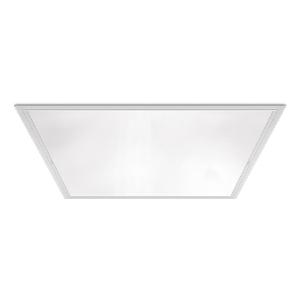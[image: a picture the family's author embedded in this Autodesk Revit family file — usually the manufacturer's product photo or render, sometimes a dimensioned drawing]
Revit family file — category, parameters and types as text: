
# Revit family: 3f_filippi_-_l_340_luce_diffusa_lgs_ip65v_3f_filippi_-_24000_-_l_340_29w-940_dali_lgs_ip65v_596x596
name_source: partatom
category: Lighting Fixtures
units: mm (PartAtom-declared; Revit-internal decimal feet)

## family parameters
Cut with Voids When Loaded = No
Host = Face
Light Source = No
Part Type = Normal
Room Calculation Point = No
Round Connector Dimension = Use Diameter
Shared = No

## types (1)
- 3F Filippi - L 340 Luce Diffusa LGS IP65V (1 x LED, 3413 lm, 35 W, 4000 K)
    Apparent Load = 35 VA
    Approval mark = ENEC
    CIE Flux Codes = 67 92 98 100 100
    Color Rendering = 90
    Color Temperature = 4000 K
    Control Gear = Electronic transformer
    Default Elevation = 1800 mm
    Description = ILLUMINOTECHNICAL
Luminous efficiency 100% (DLOR 100%, ULOR 0%).
Initial luminous flux of the luminaire 3413 lm.
Direct symmetric distribution.
Installation Interdistance Transv.D = 1.19 x hu - Long.D = 1.17 x hu.
Average luminance <1500 cd/m² for radial angles >65°.
Tabular UGR (CIE 117 - 4H-8H; S=0.25H; 70/50/20): RUG 16 - 16.1.
Beam angle: 87° - 86°.
Luminous efficacy 98 lm/W.
Lifetime (L93/B10): 30000 h. (tq+25°C)
Lifetime (L90/B10): 50000 h. (tq+25°C)
Lifetime (L85/B10): 80000 h. (tq+25°C)
Lifetime (L80/B10): 100000 h. (tq+25°C)
Sudden decreased luminous flux after 50000 hours: 0% (C0).
Photobiological safety in compliance with IEC/TR 62778: RG0 risk exempt, (IEC 62471).
In compliance with IEC/EN 62722-2-1 - IEC/EN 62717 standards.

SOURCE
Squared LED module 29W/940.
Energy efficiency class (UE 2019/2020 - UE 2019/2015): D.
CIE 13.3 Colour rendering index: CRI >90 (R9 >50%).
IES TM-30 Fidelity Index: Rf = 92 Rg = 101.
CCT nominal colour temperature 4000 K.
Colour initial tolerance (MacAdam): SDCM 3.

MECHANICAL
Housing in hot-galvanised steel, painted in white polyester.
Perimetral frame in white polycarbonate.
LGS micro-prismatic flat diffuser in transparent methacrylate (PMMA), multi-lenticular exterior, anti-glare.
Anti-glare opal polycarbonate filter for brightness uniformity.
Luminaire with limited surface temperature. - D - (EN 60598-2-24)
Dimensions: 596x596 mm, height 80 mm. Weight 4.45 kg.
IP65 protection degree for exposed part, IP40 for recessed part.
Mechanical strength to impacts IK06 (1 joule).
Glow-wire test resistance 650°C.

ELECTRICAL
Wiring on a separate unit.
Halogen Free DALI-2 DATI (Parts 251, 252, 253), PUSH-DIM, electronic wiring 230V-50/60Hz, power factor 0.95 at full load, THD <25%, constant output current, SELV, class II, 1 driver, 1 DALI addresse.
Power of the luminaire 35 W.
CE - IEC 60598-1 - EN 60598-1.
SAFE FLICKER: PstLM=<1 and SVM=<0.4 (IEC TR 61547-1 and IEC TR 63158), to ensure a more comfortable and safe light.
Luminaire compliant with EN 60598-2-22 for power supply from a centralised emergency system CPSS (Central Power Supply System), not incorporated in the luminaire - high risk areas excluded. The default power and flux are 100% in AC and 100% in DC.
Ambient temperature from 0°C to +40°C.
Temperature class T6 max 85°C.
Relative humidity UR: <85%.

INSTALLATION
Lay-on or pull-up recessed fitting using frame accessory.
All accessories dedicated to this product are available on the Catalog and on our website www.3F-Filippi.com.

APPLICATIONS
Suitable product for food production plants (HACCP), IFS (Food Version 6), BRC (GSFS Food Version 7).
In environments requiring protection and simplified cleaning.
Hospitals, pharmaceutical, chemical, aseptic laboratories, sterilised rooms.
Environments: with VDTs, meeting rooms, offices.
Environments: architectural, commercial, staterooms, banks.
Environments where demanding visual tasks are performed and soft diffuse light is required for optimal visual comfort and total shielding of the light source.

LIGHT MANAGEMENT
Recommended minimum setting: 10%.
The luminaire, equipped with (DALI-2 DATI) driver, can be controlled manually with 3F Easy Dim technology or automatically/manually with wired or wireless DALI/D2D control systems.
The D2D driver guarantees interoperability with other devices with the same certification by making the following information available:
Device Data (Part 251), Energy Report (Part 252), Diagnosis & Maintenance (Part 253).
In electrical systems without a regulation system (manual or automatic) and DALI bus, a suitable jumper must be made on the DA-DA terminals of the appliance.

WARNING
Luminaire designed for disposal/recycling at end-of-life.
Replaceable (LED only) light source by a professional. Replaceable control gear by a professional.
    Height = 0 mm  [stored 0 ft]
    Lamp = 1 x LED
    Lamp Light Flux = 3413 lm
    Lamp Power = 35 W
    Lamp count = 1
    Length = 596 mm
    Lifetime = 50000 h
    Luminous efficacy = 98 lm/W
    Manufacturer = 3F Filippi
    ModVariant = No
    Model = 3F Filippi - 24000 - L 340 29W-940 DALI LGS IP65V 596x596
    Mounting Place = Ceiling
    Mounting Type = Recessed
    Number of Poles = 1
    OnlyDefault = Yes
    Power Factor = 1
    Product Name = 3F Filippi - L 340 Luce Diffusa LGS IP65V
    Product group = recessed luminaire
    ProductGroupID = 4
    Protection Class = Protection class II
    Protection Degree = IP 40
    RLX_Detail_Level = 1
    RLX_Emergency_Light_Flux = 0 lm
    RLX_Emergency_Type = 0
    RLX_Emergency_Type_DB = No
    RlxData = <blob elided: 155929 chars, md5=2735b36f>
    Socket = socket
    Standby Power = 0 W
    System Light Flux = 3413 lm
    System Power = 35 W
    Type Comments = Product without accessories
    Type Image = 3ffilippi_l_340_luce_diffusa_lgs_ip65v.jpg
    URL = http://relux.com
    VarID = ---
    Voltage = 0 V
    Weight = 0.00 kg
    Width = 596 mm

note: [stored X ft] marks values corroborated as IEEE doubles in the binary element streams (Revit-internal decimal feet)

## geometry (parser evidence)
native form markers: Blend x4, Sweep x10
no freeform markers — native parametric forms only
